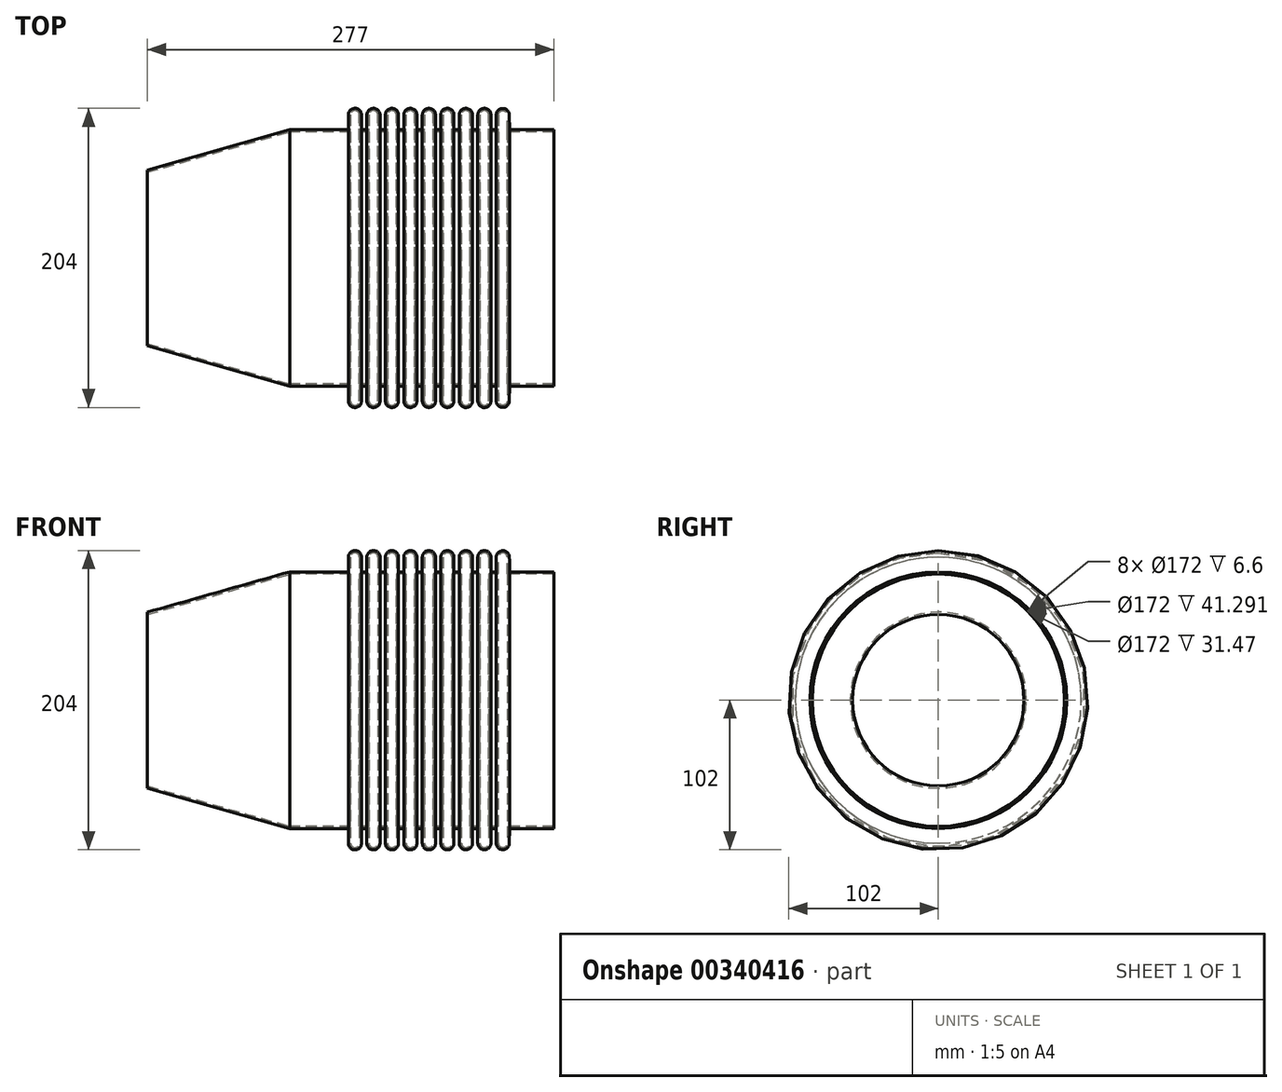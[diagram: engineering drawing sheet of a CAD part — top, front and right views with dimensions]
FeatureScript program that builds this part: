
annotation { "Feature Type Name" : "Feature", "Feature Type Description" : "" }
export const myFeature = defineFeature(function(context is Context, id is Id, definition is map)
    precondition{}
    {
        {
            var Q0;
            Q0=qCreatedBy(makeId("Front.planeOp"),FACE);
            var sketch = newSketch(context, id + "F0", { "sketchPlane" : qUnion([Q0])});
            skLineSegment(sketch, "E0", {"start": v(-141.3, 0) * mm, "end": v(135.7, 0) * mm});
            skLineSegment(sketch, "E1", {"start": v(-141.3, 0) * mm, "end": v(-141.3, 60) * mm});
            skLineSegment(sketch, "E2", {"start": v(135.7, 0) * mm, "end": v(135.7, 87.5) * mm});
            skLineSegment(sketch, "E3", {"start": v(135.7, 87.5) * mm, "end": v(105.7, 87.5) * mm});
            skLineSegment(sketch, "E4", {"start": v(-4.3, 97.5) * mm, "end": v(-4.3, 87.5) * mm});
            skLineSegment(sketch, "E5", {"start": v(-4.3, 87.5) * mm, "end": v(-44.3, 87.5) * mm});
            skLineSegment(sketch, "E6", {"start": v(-44.3, 87.5) * mm, "end": v(-141.3, 60) * mm});
            skLineSegment(sketch, "E7", {"start": v(4.7, 87.5) * mm, "end": v(8.3, 87.5) * mm});
            skLineSegment(sketch, "E8", {"start": v(4.7, 97.5) * mm, "end": v(4.7, 87.5) * mm});
            skPoint(sketch, "E8.endSnap0", {"position": v(-24.3, 87.5) * mm});
            skLineSegment(sketch, "E9", {"start": v(8.3, 97.5) * mm, "end": v(8.3, 87.5) * mm});
            skLineSegment(sketch, "E10", {"start": v(17.3, 97.5) * mm, "end": v(17.3, 87.5) * mm});
            skLineSegment(sketch, "E11", {"start": v(20.9, 87.5) * mm, "end": v(20.9, 97.5) * mm});
            skLineSegment(sketch, "E12", {"start": v(29.9, 97.5) * mm, "end": v(29.9, 87.5) * mm});
            skLineSegment(sketch, "E13", {"start": v(33.5, 97.5) * mm, "end": v(33.5, 87.5) * mm});
            skLineSegment(sketch, "E14", {"start": v(42.5, 97.5) * mm, "end": v(42.5, 87.5) * mm});
            skLineSegment(sketch, "E15", {"start": v(46.1, 97.5) * mm, "end": v(46.1, 87.5) * mm});
            skLineSegment(sketch, "E16", {"start": v(55.1, 97.5) * mm, "end": v(55.1, 87.5) * mm});
            skLineSegment(sketch, "E17", {"start": v(58.7, 97.5) * mm, "end": v(58.7, 87.5) * mm});
            skLineSegment(sketch, "E18", {"start": v(67.7, 97.5) * mm, "end": v(67.7, 87.5) * mm});
            skLineSegment(sketch, "E19", {"start": v(71.3, 97.5) * mm, "end": v(71.3, 87.5) * mm});
            skLineSegment(sketch, "E20", {"start": v(80.3, 97.5) * mm, "end": v(80.3, 87.5) * mm});
            skLineSegment(sketch, "E21", {"start": v(83.9, 97.5) * mm, "end": v(83.9, 87.5) * mm});
            skLineSegment(sketch, "E22", {"start": v(92.9, 97.5) * mm, "end": v(92.9, 87.5) * mm});
            skLineSegment(sketch, "E23", {"start": v(96.5, 97.5) * mm, "end": v(96.5, 87.5) * mm});
            skLineSegment(sketch, "E24", {"start": v(105.5, 97.5) * mm, "end": v(105.7, 87.5) * mm});
            skArc(sketch, "E25", {"start": v(4.7, 97.5) * mm, "mid": v(0.2, 102) * mm, "end": v(-4.3, 97.5) * mm});
            skArc(sketch, "E26", {"start": v(17.3, 97.5) * mm, "mid": v(12.8, 102) * mm, "end": v(8.3, 97.5) * mm});
            skArc(sketch, "E27", {"start": v(29.9, 97.5) * mm, "mid": v(25.4, 102) * mm, "end": v(20.9, 97.5) * mm});
            skArc(sketch, "E28", {"start": v(42.5, 97.5) * mm, "mid": v(38, 102) * mm, "end": v(33.5, 97.5) * mm});
            skArc(sketch, "E29", {"start": v(55.1, 97.5) * mm, "mid": v(50.6, 102) * mm, "end": v(46.1, 97.5) * mm});
            skArc(sketch, "E30", {"start": v(67.7, 97.5) * mm, "mid": v(63.2, 102) * mm, "end": v(58.7, 97.5) * mm});
            skArc(sketch, "E31", {"start": v(80.3, 97.5) * mm, "mid": v(75.8, 102) * mm, "end": v(71.3, 97.5) * mm});
            skArc(sketch, "E32", {"start": v(92.9, 97.5) * mm, "mid": v(88.4, 102) * mm, "end": v(83.9, 97.5) * mm});
            skArc(sketch, "E33", {"start": v(105.5, 97.5) * mm, "mid": v(101, 101.91) * mm, "end": v(96.5, 97.5) * mm});
            skLineSegment(sketch, "E34.trimOffspring", {"start": v(17.3, 87.5) * mm, "end": v(20.9, 87.5) * mm});
            skLineSegment(sketch, "E35.trimOffspring", {"start": v(29.9, 87.5) * mm, "end": v(33.5, 87.5) * mm});
            skLineSegment(sketch, "E36.trimOffspring", {"start": v(42.5, 87.5) * mm, "end": v(46.1, 87.5) * mm});
            skLineSegment(sketch, "E37.trimOffspring", {"start": v(55.1, 87.5) * mm, "end": v(58.7, 87.5) * mm});
            skLineSegment(sketch, "E38.trimOffspring", {"start": v(67.7, 87.5) * mm, "end": v(71.3, 87.5) * mm});
            skLineSegment(sketch, "E39.trimOffspring", {"start": v(80.3, 87.5) * mm, "end": v(83.9, 87.5) * mm});
            skLineSegment(sketch, "E40.trimOffspring", {"start": v(92.9, 87.5) * mm, "end": v(96.5, 87.5) * mm});
            skSolve(sketch);
        }
        {
            var Q0;
            Q0 = qSketchRegion(id + "F0", true);
            var Q1;
            Q1=sQuery(id+"F0.wireOp",EDGE,"E0");
            revolve(context, id + "F1", {"entities" : qUnion([Q0]), "axis" : qUnion([Q1]), "revolveType" : RevolveType.FULL});
        }
        {
            var Q0;
            Q0=makeQuery(id+"F1.opRevolve","SWEPT_FACE",FACE,{"disambiguationData":[OSD([sQuery(id+"F0.wireOp",EDGE,"E2")])]});
            var Q1;
            Q1=makeQuery(id+"F1.opRevolve","SWEPT_FACE",FACE,{"disambiguationData":[OSD([sQuery(id+"F0.wireOp",EDGE,"E1")])]});
            shell(context, id + "F2", {"entities" : qUnion([Q0, Q1]), "thickness" : 1.5 * mm});
        }
    });
